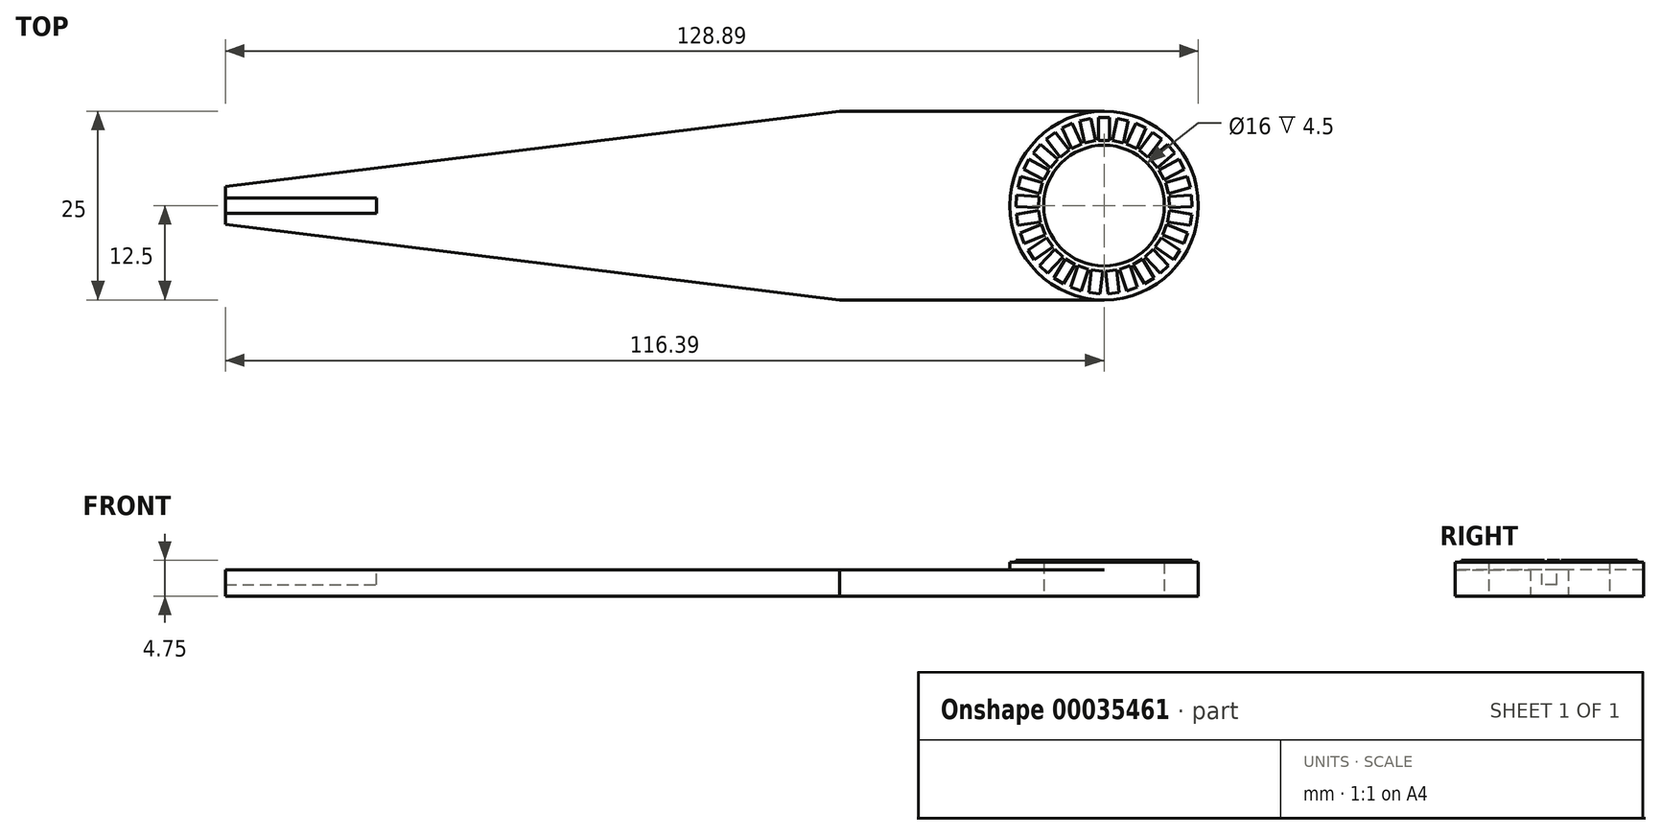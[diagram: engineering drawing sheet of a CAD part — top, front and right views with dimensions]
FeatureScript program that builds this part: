
annotation { "Feature Type Name" : "Feature", "Feature Type Description" : "" }
export const myFeature = defineFeature(function(context is Context, id is Id, definition is map)
    precondition{}
    {
        {
            var Q0;
            Q0=qCreatedBy(makeId("Top.planeOp"),FACE);
            var sketch = newSketch(context, id + "F0", { "sketchPlane" : qUnion([Q0])});
            skCircle(sketch, "E0", {"center": v(0, 0) * mm, "radius": 8 * mm});
            skCircle(sketch, "E1", {"center": v(0, 0) * mm, "radius": 12.5 * mm});
            skLineSegment(sketch, "E2", {"start": v(-35, 12.5) * mm, "end": v(0, 12.5) * mm});
            skLineSegment(sketch, "E3", {"start": v(-35, -12.5) * mm, "end": v(0, -12.5) * mm});
            skLineSegment(sketch, "E4", {"start": v(-35, 12.5) * mm, "end": v(-121.4, 12.5) * mm, "construction": true});
            skLineSegment(sketch, "E5", {"start": v(-35, 12.5) * mm, "end": v(-116.39, 2.5) * mm});
            skLineSegment(sketch, "E6", {"start": v(-35, -12.5) * mm, "end": v(-123.46, -12.5) * mm, "construction": true});
            skLineSegment(sketch, "E7", {"start": v(-35, -12.5) * mm, "end": v(-116.39, -2.5) * mm});
            skLineSegment(sketch, "E8", {"start": v(-116.39, 2.5) * mm, "end": v(-116.39, -2.5) * mm});
            skSolve(sketch);
        }
        {
            var Q0;
            Q0 = qSketchRegion(id + "F0", true);
            extrude(context, id + "F1", {"entities" : qUnion([Q0]), "depth" : 3.5 * mm});
        }
        {
            var Q0;
            Q0=makeQuery(id+"F1.opExtrude","CAP_FACE",FACE,{"disambiguationData":[OSD([sQuery(id+"F0.wireOp",EDGE,"E0"),sQuery(id+"F0.wireOp",EDGE,"E1"),sQuery(id+"F0.wireOp",EDGE,"E2"),sQuery(id+"F0.wireOp",EDGE,"E3"),sQuery(id+"F0.wireOp",EDGE,"E5"),sQuery(id+"F0.wireOp",EDGE,"E7"),sQuery(id+"F0.wireOp",EDGE,"E8")])],"isStart":false});
            var sketch = newSketch(context, id + "F2", { "sketchPlane" : qUnion([Q0])});
            skCircle(sketch, "E9", {"center": v(0, 0) * mm, "radius": 12.5 * mm});
            skCircle(sketch, "E10", {"center": v(0, 0) * mm, "radius": 8 * mm});
            skSolve(sketch);
        }
        {
            var Q0;
            Q0 = qSketchRegion(id + "F2", true);
            extrude(context, id + "F3", {"entities" : qUnion([Q0]), "operationType" : NewBodyOperationType.ADD, "depth" : 1 * mm});
        }
        {
            var Q0;
            Q0=makeQuery(id+"F1.opExtrude","CAP_FACE",FACE,{"disambiguationData":[OSD([sQuery(id+"F0.wireOp",EDGE,"E0"),sQuery(id+"F0.wireOp",EDGE,"E1"),sQuery(id+"F0.wireOp",EDGE,"E2"),sQuery(id+"F0.wireOp",EDGE,"E3"),sQuery(id+"F0.wireOp",EDGE,"E5"),sQuery(id+"F0.wireOp",EDGE,"E7"),sQuery(id+"F0.wireOp",EDGE,"E8")])],"isStart":false});
            var sketch = newSketch(context, id + "F4", { "sketchPlane" : qUnion([Q0])});
            skLineSegment(sketch, "E11.bottom", {"start": v(-116.39, 1) * mm, "end": v(-96.39, 1) * mm});
            skLineSegment(sketch, "E11.top", {"start": v(-116.39, -1) * mm, "end": v(-96.39, -1) * mm});
            skLineSegment(sketch, "E11.left", {"start": v(-116.39, 1) * mm, "end": v(-116.39, -1) * mm});
            skLineSegment(sketch, "E11.right", {"start": v(-96.39, 1) * mm, "end": v(-96.39, -1) * mm});
            skSolve(sketch);
        }
        {
            var Q0;
            Q0 = qSketchRegion(id + "F4", true);
            extrude(context, id + "F5", {"entities" : qUnion([Q0]), "operationType" : NewBodyOperationType.REMOVE, "oppositeDirection" : true, "depth" : 2 * mm});
        }
        {
            var Q0;
            Q0=makeQuery(id+"F3.opExtrude","CAP_FACE",FACE,{"disambiguationData":[OSD([sQuery(id+"F2.wireOp",EDGE,"E9"),sQuery(id+"F2.wireOp",EDGE,"E10")])],"isStart":false});
            var sketch = newSketch(context, id + "F6", { "sketchPlane" : qUnion([Q0])});
            skLineSegment(sketch, "E12.bottom", {"start": v(-0.75, 11.65) * mm, "end": v(0.75, 11.65) * mm});
            skLineSegment(sketch, "E12.top", {"start": v(-0.75, 8.65) * mm, "end": v(0.75, 8.65) * mm});
            skLineSegment(sketch, "E12.left", {"start": v(-0.75, 11.65) * mm, "end": v(-0.75, 8.65) * mm});
            skLineSegment(sketch, "E12.right", {"start": v(0.75, 11.65) * mm, "end": v(0.75, 8.65) * mm});
            skLineSegment(sketch, "E13.1.0", {"start": v(1.77, 11.54) * mm, "end": v(1.13, 8.61) * mm});
            skLineSegment(sketch, "E13.1.1", {"start": v(1.13, 8.61) * mm, "end": v(2.6, 8.29) * mm});
            skLineSegment(sketch, "E13.1.2", {"start": v(1.77, 11.54) * mm, "end": v(3.24, 11.22) * mm});
            skLineSegment(sketch, "E13.1.3", {"start": v(3.24, 11.22) * mm, "end": v(2.6, 8.29) * mm});
            skLineSegment(sketch, "E13.2.0", {"start": v(4.21, 10.9) * mm, "end": v(2.95, 8.17) * mm});
            skLineSegment(sketch, "E13.2.1", {"start": v(2.95, 8.17) * mm, "end": v(4.31, 7.54) * mm});
            skLineSegment(sketch, "E13.2.2", {"start": v(4.21, 10.9) * mm, "end": v(5.57, 10.26) * mm});
            skLineSegment(sketch, "E13.2.3", {"start": v(5.57, 10.26) * mm, "end": v(4.31, 7.54) * mm});
            skLineSegment(sketch, "E13.3.0", {"start": v(6.46, 9.73) * mm, "end": v(4.64, 7.34) * mm});
            skLineSegment(sketch, "E13.3.1", {"start": v(4.64, 7.34) * mm, "end": v(5.83, 6.43) * mm});
            skLineSegment(sketch, "E13.3.2", {"start": v(6.46, 9.73) * mm, "end": v(7.65, 8.82) * mm});
            skLineSegment(sketch, "E13.3.3", {"start": v(7.65, 8.82) * mm, "end": v(5.83, 6.43) * mm});
            skLineSegment(sketch, "E13.4.0", {"start": v(8.4, 8.12) * mm, "end": v(6.1, 6.17) * mm});
            skLineSegment(sketch, "E13.4.1", {"start": v(6.1, 6.17) * mm, "end": v(7.08, 5.03) * mm});
            skLineSegment(sketch, "E13.4.2", {"start": v(8.4, 8.12) * mm, "end": v(9.37, 6.97) * mm});
            skLineSegment(sketch, "E13.4.3", {"start": v(9.37, 6.97) * mm, "end": v(7.08, 5.03) * mm});
            skLineSegment(sketch, "E13.5.0", {"start": v(9.94, 6.12) * mm, "end": v(7.3, 4.72) * mm});
            skLineSegment(sketch, "E13.5.1", {"start": v(7.3, 4.72) * mm, "end": v(8, 3.4) * mm});
            skLineSegment(sketch, "E13.5.2", {"start": v(9.94, 6.12) * mm, "end": v(10.65, 4.8) * mm});
            skLineSegment(sketch, "E13.5.3", {"start": v(10.65, 4.8) * mm, "end": v(8, 3.4) * mm});
            skLineSegment(sketch, "E13.6.0", {"start": v(11.03, 3.84) * mm, "end": v(8.14, 3.04) * mm});
            skLineSegment(sketch, "E13.6.1", {"start": v(8.14, 3.04) * mm, "end": v(8.54, 1.6) * mm});
            skLineSegment(sketch, "E13.6.2", {"start": v(11.03, 3.84) * mm, "end": v(11.43, 2.4) * mm});
            skLineSegment(sketch, "E13.6.3", {"start": v(11.43, 2.4) * mm, "end": v(8.54, 1.6) * mm});
            skLineSegment(sketch, "E13.7.0", {"start": v(11.6, 1.38) * mm, "end": v(8.6, 1.22) * mm});
            skLineSegment(sketch, "E13.7.1", {"start": v(8.6, 1.22) * mm, "end": v(8.68, -0.28) * mm});
            skLineSegment(sketch, "E13.7.2", {"start": v(11.6, 1.38) * mm, "end": v(11.68, -0.12) * mm});
            skLineSegment(sketch, "E13.7.3", {"start": v(11.68, -0.12) * mm, "end": v(8.68, -0.28) * mm});
            skLineSegment(sketch, "E13.8.0", {"start": v(11.62, -1.15) * mm, "end": v(8.66, -0.66) * mm});
            skLineSegment(sketch, "E13.8.1", {"start": v(8.66, -0.66) * mm, "end": v(8.42, -2.14) * mm});
            skLineSegment(sketch, "E13.8.2", {"start": v(11.62, -1.15) * mm, "end": v(11.38, -2.63) * mm});
            skLineSegment(sketch, "E13.8.3", {"start": v(11.38, -2.63) * mm, "end": v(8.42, -2.14) * mm});
            skLineSegment(sketch, "E13.9.0", {"start": v(11.1, -3.62) * mm, "end": v(8.32, -2.5) * mm});
            skLineSegment(sketch, "E13.9.1", {"start": v(8.32, -2.5) * mm, "end": v(7.76, -3.9) * mm});
            skLineSegment(sketch, "E13.9.2", {"start": v(11.1, -3.62) * mm, "end": v(10.55, -5.01) * mm});
            skLineSegment(sketch, "E13.9.3", {"start": v(10.55, -5.01) * mm, "end": v(7.76, -3.9) * mm});
            skLineSegment(sketch, "E13.10.0", {"start": v(10.07, -5.92) * mm, "end": v(7.58, -4.24) * mm});
            skLineSegment(sketch, "E13.10.1", {"start": v(7.58, -4.24) * mm, "end": v(6.74, -5.48) * mm});
            skLineSegment(sketch, "E13.10.2", {"start": v(10.07, -5.92) * mm, "end": v(9.22, -7.16) * mm});
            skLineSegment(sketch, "E13.10.3", {"start": v(9.22, -7.16) * mm, "end": v(6.74, -5.48) * mm});
            skLineSegment(sketch, "E13.11.0", {"start": v(8.56, -7.94) * mm, "end": v(6.5, -5.77) * mm});
            skLineSegment(sketch, "E13.11.1", {"start": v(6.5, -5.77) * mm, "end": v(5.4, -6.8) * mm});
            skLineSegment(sketch, "E13.11.2", {"start": v(8.56, -7.94) * mm, "end": v(7.47, -8.98) * mm});
            skLineSegment(sketch, "E13.11.3", {"start": v(7.47, -8.98) * mm, "end": v(5.4, -6.8) * mm});
            skLineSegment(sketch, "E13.12.0", {"start": v(6.65, -9.6) * mm, "end": v(5.1, -7.03) * mm});
            skLineSegment(sketch, "E13.12.1", {"start": v(5.1, -7.03) * mm, "end": v(3.82, -7.8) * mm});
            skLineSegment(sketch, "E13.12.2", {"start": v(6.65, -9.6) * mm, "end": v(5.37, -10.37) * mm});
            skLineSegment(sketch, "E13.12.3", {"start": v(5.37, -10.37) * mm, "end": v(3.82, -7.8) * mm});
            skLineSegment(sketch, "E13.13.0", {"start": v(4.43, -10.8) * mm, "end": v(3.47, -7.96) * mm});
            skLineSegment(sketch, "E13.13.1", {"start": v(3.47, -7.96) * mm, "end": v(2.05, -8.44) * mm});
            skLineSegment(sketch, "E13.13.2", {"start": v(4.43, -10.8) * mm, "end": v(3.01, -11.28) * mm});
            skLineSegment(sketch, "E13.13.3", {"start": v(3.01, -11.28) * mm, "end": v(2.05, -8.44) * mm});
            skLineSegment(sketch, "E13.14.0", {"start": v(2, -11.5) * mm, "end": v(1.68, -8.52) * mm});
            skLineSegment(sketch, "E13.14.1", {"start": v(1.68, -8.52) * mm, "end": v(0.19, -8.68) * mm});
            skLineSegment(sketch, "E13.14.2", {"start": v(2, -11.5) * mm, "end": v(0.51, -11.67) * mm});
            skLineSegment(sketch, "E13.14.3", {"start": v(0.51, -11.67) * mm, "end": v(0.19, -8.68) * mm});
            skLineSegment(sketch, "E13.15.0", {"start": v(-0.51, -11.67) * mm, "end": v(-0.19, -8.68) * mm});
            skLineSegment(sketch, "E13.15.1", {"start": v(-0.19, -8.68) * mm, "end": v(-1.68, -8.52) * mm});
            skLineSegment(sketch, "E13.15.2", {"start": v(-0.51, -11.67) * mm, "end": v(-2, -11.5) * mm});
            skLineSegment(sketch, "E13.15.3", {"start": v(-2, -11.5) * mm, "end": v(-1.68, -8.52) * mm});
            skLineSegment(sketch, "E13.16.0", {"start": v(-3.01, -11.28) * mm, "end": v(-2.05, -8.44) * mm});
            skLineSegment(sketch, "E13.16.1", {"start": v(-2.05, -8.44) * mm, "end": v(-3.47, -7.96) * mm});
            skLineSegment(sketch, "E13.16.2", {"start": v(-3.01, -11.28) * mm, "end": v(-4.43, -10.8) * mm});
            skLineSegment(sketch, "E13.16.3", {"start": v(-4.43, -10.8) * mm, "end": v(-3.47, -7.96) * mm});
            skLineSegment(sketch, "E13.17.0", {"start": v(-5.37, -10.37) * mm, "end": v(-3.82, -7.8) * mm});
            skLineSegment(sketch, "E13.17.1", {"start": v(-3.82, -7.8) * mm, "end": v(-5.1, -7.03) * mm});
            skLineSegment(sketch, "E13.17.2", {"start": v(-5.37, -10.37) * mm, "end": v(-6.65, -9.6) * mm});
            skLineSegment(sketch, "E13.17.3", {"start": v(-6.65, -9.6) * mm, "end": v(-5.1, -7.03) * mm});
            skLineSegment(sketch, "E13.18.0", {"start": v(-7.47, -8.98) * mm, "end": v(-5.4, -6.8) * mm});
            skLineSegment(sketch, "E13.18.1", {"start": v(-5.4, -6.8) * mm, "end": v(-6.5, -5.77) * mm});
            skLineSegment(sketch, "E13.18.2", {"start": v(-7.47, -8.98) * mm, "end": v(-8.56, -7.94) * mm});
            skLineSegment(sketch, "E13.18.3", {"start": v(-8.56, -7.94) * mm, "end": v(-6.5, -5.77) * mm});
            skLineSegment(sketch, "E13.19.0", {"start": v(-9.22, -7.16) * mm, "end": v(-6.74, -5.48) * mm});
            skLineSegment(sketch, "E13.19.1", {"start": v(-6.74, -5.48) * mm, "end": v(-7.58, -4.24) * mm});
            skLineSegment(sketch, "E13.19.2", {"start": v(-9.22, -7.16) * mm, "end": v(-10.07, -5.92) * mm});
            skLineSegment(sketch, "E13.19.3", {"start": v(-10.07, -5.92) * mm, "end": v(-7.58, -4.24) * mm});
            skLineSegment(sketch, "E13.20.0", {"start": v(-10.55, -5.01) * mm, "end": v(-7.76, -3.9) * mm});
            skLineSegment(sketch, "E13.20.1", {"start": v(-7.76, -3.9) * mm, "end": v(-8.32, -2.5) * mm});
            skLineSegment(sketch, "E13.20.2", {"start": v(-10.55, -5.01) * mm, "end": v(-11.1, -3.62) * mm});
            skLineSegment(sketch, "E13.20.3", {"start": v(-11.1, -3.62) * mm, "end": v(-8.32, -2.5) * mm});
            skLineSegment(sketch, "E13.21.0", {"start": v(-11.38, -2.63) * mm, "end": v(-8.42, -2.14) * mm});
            skLineSegment(sketch, "E13.21.1", {"start": v(-8.42, -2.14) * mm, "end": v(-8.66, -0.66) * mm});
            skLineSegment(sketch, "E13.21.2", {"start": v(-11.38, -2.63) * mm, "end": v(-11.62, -1.15) * mm});
            skLineSegment(sketch, "E13.21.3", {"start": v(-11.62, -1.15) * mm, "end": v(-8.66, -0.66) * mm});
            skLineSegment(sketch, "E13.22.0", {"start": v(-11.68, -0.12) * mm, "end": v(-8.68, -0.28) * mm});
            skLineSegment(sketch, "E13.22.1", {"start": v(-8.68, -0.28) * mm, "end": v(-8.6, 1.22) * mm});
            skLineSegment(sketch, "E13.22.2", {"start": v(-11.68, -0.12) * mm, "end": v(-11.6, 1.38) * mm});
            skLineSegment(sketch, "E13.22.3", {"start": v(-11.6, 1.38) * mm, "end": v(-8.6, 1.22) * mm});
            skLineSegment(sketch, "E13.23.0", {"start": v(-11.43, 2.4) * mm, "end": v(-8.54, 1.6) * mm});
            skLineSegment(sketch, "E13.23.1", {"start": v(-8.54, 1.6) * mm, "end": v(-8.14, 3.04) * mm});
            skLineSegment(sketch, "E13.23.2", {"start": v(-11.43, 2.4) * mm, "end": v(-11.03, 3.84) * mm});
            skLineSegment(sketch, "E13.23.3", {"start": v(-11.03, 3.84) * mm, "end": v(-8.14, 3.04) * mm});
            skLineSegment(sketch, "E13.24.0", {"start": v(-10.65, 4.8) * mm, "end": v(-8, 3.4) * mm});
            skLineSegment(sketch, "E13.24.1", {"start": v(-8, 3.4) * mm, "end": v(-7.3, 4.72) * mm});
            skLineSegment(sketch, "E13.24.2", {"start": v(-10.65, 4.8) * mm, "end": v(-9.94, 6.12) * mm});
            skLineSegment(sketch, "E13.24.3", {"start": v(-9.94, 6.12) * mm, "end": v(-7.3, 4.72) * mm});
            skLineSegment(sketch, "E13.25.0", {"start": v(-9.37, 6.97) * mm, "end": v(-7.08, 5.03) * mm});
            skLineSegment(sketch, "E13.25.1", {"start": v(-7.08, 5.03) * mm, "end": v(-6.1, 6.17) * mm});
            skLineSegment(sketch, "E13.25.2", {"start": v(-9.37, 6.97) * mm, "end": v(-8.4, 8.12) * mm});
            skLineSegment(sketch, "E13.25.3", {"start": v(-8.4, 8.12) * mm, "end": v(-6.1, 6.17) * mm});
            skLineSegment(sketch, "E13.26.0", {"start": v(-7.65, 8.82) * mm, "end": v(-5.83, 6.43) * mm});
            skLineSegment(sketch, "E13.26.1", {"start": v(-5.83, 6.43) * mm, "end": v(-4.64, 7.34) * mm});
            skLineSegment(sketch, "E13.26.2", {"start": v(-7.65, 8.82) * mm, "end": v(-6.46, 9.73) * mm});
            skLineSegment(sketch, "E13.26.3", {"start": v(-6.46, 9.73) * mm, "end": v(-4.64, 7.34) * mm});
            skLineSegment(sketch, "E13.27.0", {"start": v(-5.57, 10.26) * mm, "end": v(-4.31, 7.54) * mm});
            skLineSegment(sketch, "E13.27.1", {"start": v(-4.31, 7.54) * mm, "end": v(-2.95, 8.17) * mm});
            skLineSegment(sketch, "E13.27.2", {"start": v(-5.57, 10.26) * mm, "end": v(-4.21, 10.9) * mm});
            skLineSegment(sketch, "E13.27.3", {"start": v(-4.21, 10.9) * mm, "end": v(-2.95, 8.17) * mm});
            skLineSegment(sketch, "E13.28.0", {"start": v(-3.24, 11.22) * mm, "end": v(-2.6, 8.29) * mm});
            skLineSegment(sketch, "E13.28.1", {"start": v(-2.6, 8.29) * mm, "end": v(-1.13, 8.61) * mm});
            skLineSegment(sketch, "E13.28.2", {"start": v(-3.24, 11.22) * mm, "end": v(-1.77, 11.54) * mm});
            skLineSegment(sketch, "E13.28.3", {"start": v(-1.77, 11.54) * mm, "end": v(-1.13, 8.61) * mm});
            skPoint(sketch, "E13.center", {"position": v(0, 0) * mm});
            skLineSegment(sketch, "E13.anchor1", {"start": v(0, 0) * mm, "end": v(-0.75, 8.65) * mm, "construction": true});
            skLineSegment(sketch, "E13.anchor2", {"start": v(0, 0) * mm, "end": v(-0.75, 8.65) * mm, "construction": true});
            skSolve(sketch);
        }
        {
            var Q0;
            Q0 = qSketchRegion(id + "F6", true);
            extrude(context, id + "F7", {"entities" : qUnion([Q0]), "operationType" : NewBodyOperationType.ADD, "depth" : .25 * mm});
        }
    });
